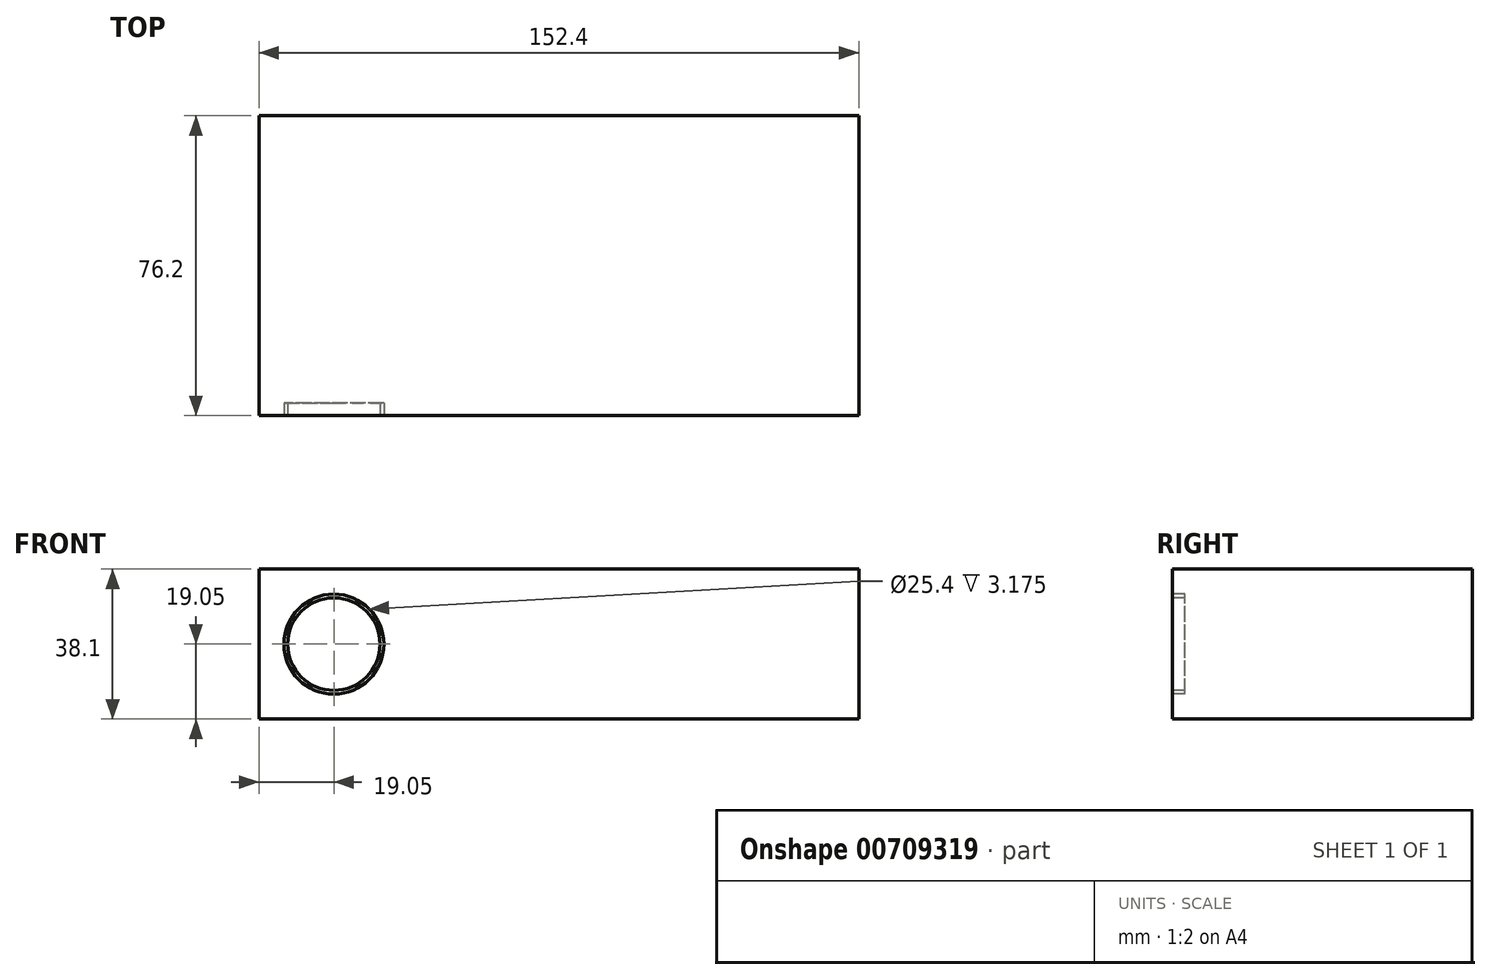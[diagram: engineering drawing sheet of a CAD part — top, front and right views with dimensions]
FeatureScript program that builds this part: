
annotation { "Feature Type Name" : "Feature", "Feature Type Description" : "" }
export const myFeature = defineFeature(function(context is Context, id is Id, definition is map)
    precondition{}
    {
        {
            var Q0;
            Q0=qCreatedBy(makeId("Front.planeOp"),FACE);
            var sketch = newSketch(context, id + "F0", { "sketchPlane" : qUnion([Q0])});
            skLineSegment(sketch, "E0.bottom", {"start": v(76.2, -19.05) * mm, "end": v(-76.2, -19.05) * mm});
            skLineSegment(sketch, "E0.top", {"start": v(76.2, 19.05) * mm, "end": v(-76.2, 19.05) * mm});
            skLineSegment(sketch, "E0.left", {"start": v(76.2, -19.05) * mm, "end": v(76.2, 19.05) * mm});
            skLineSegment(sketch, "E0.right", {"start": v(-76.2, -19.05) * mm, "end": v(-76.2, 19.05) * mm});
            skPoint(sketch, "E0.middle", {"position": v(0, 0) * mm});
            skSolve(sketch);
        }
        {
            var Q0;
            Q0=qSketchRegion(id+"F0",true);
            extrude(context, id + "F1", {"entities" : qUnion([Q0]), "depth" : 76.2 * mm, "offsetDistance" : 25.4 * mm});
        }
        {
            var Q0;
            Q0=makeQuery(id+"F1.opExtrude","CAP_FACE",FACE,{"disambiguationData":[OSD([sQuery(id+"F0.wireOp",EDGE,"E0.bottom"),sQuery(id+"F0.wireOp",EDGE,"E0.top"),sQuery(id+"F0.wireOp",EDGE,"E0.left"),sQuery(id+"F0.wireOp",EDGE,"E0.right")])],"isStart":false});
            var sketch = newSketch(context, id + "F2", { "sketchPlane" : qUnion([Q0])});
            skCircle(sketch, "E1", {"center": v(-57.15, 0) * mm, "radius": 12.7 * mm});
            skCircle(sketch, "E2", {"center": v(-57.15, 0) * mm, "radius": 11.74 * mm});
            skSolve(sketch);
        }
        {
            var Q0;
            Q0 = qSketchRegion(id + "F2", true);
            extrude(context, id + "F3", {"entities" : qUnion([Q0]), "operationType" : NewBodyOperationType.REMOVE, "oppositeDirection" : true, "depth" : 3.17 * mm, "offsetDistance" : 25.4 * mm});
        }
    });
